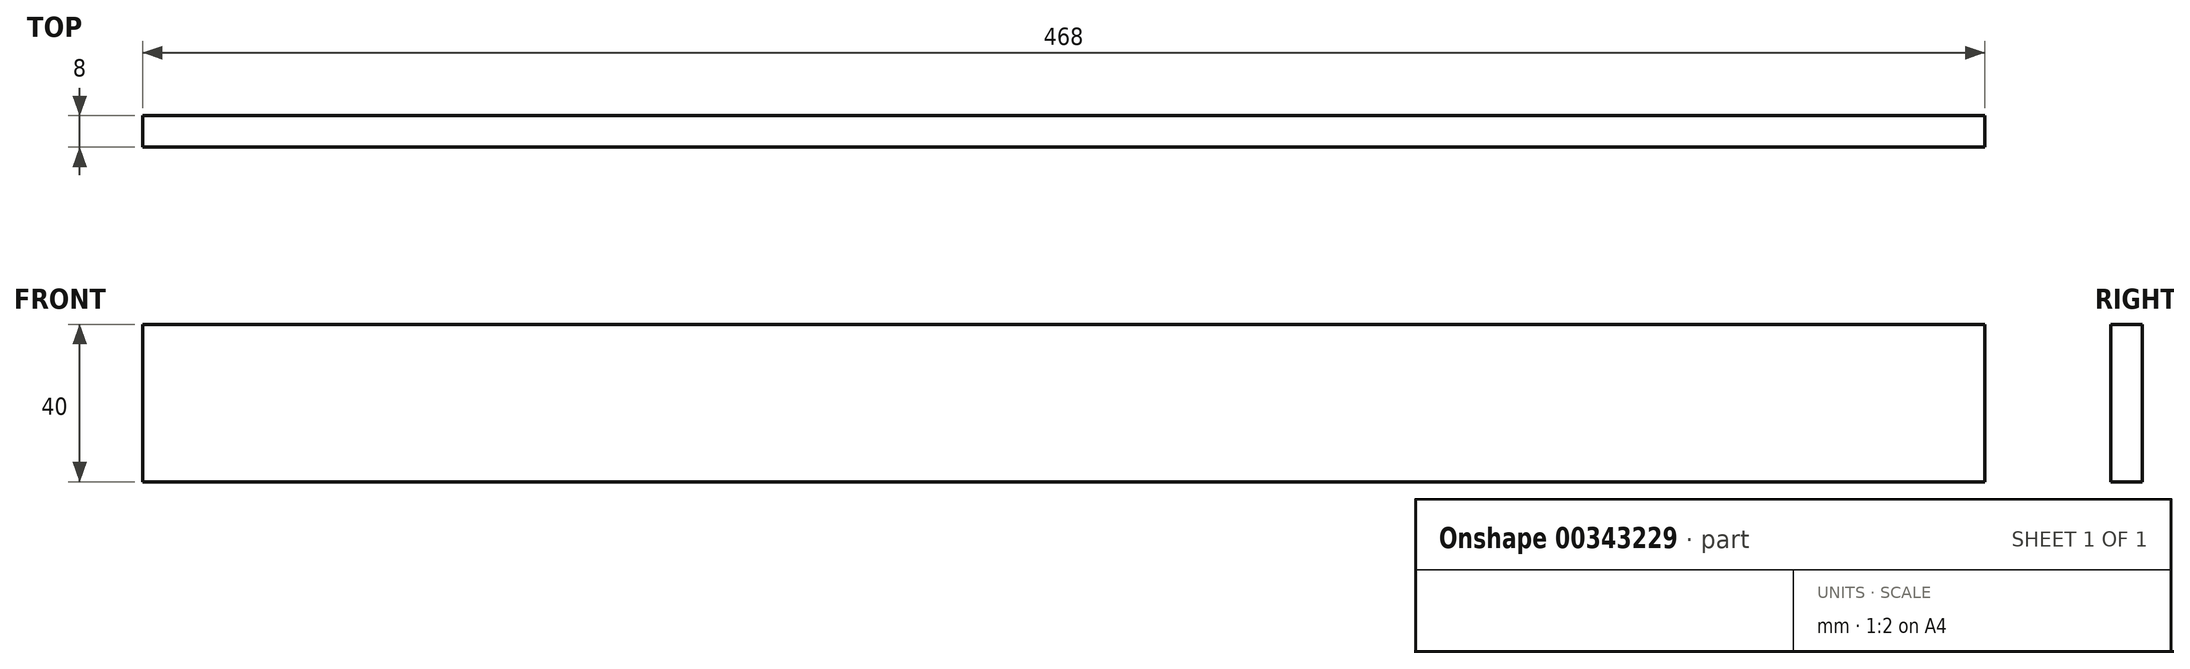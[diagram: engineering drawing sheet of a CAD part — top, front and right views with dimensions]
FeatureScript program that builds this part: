
annotation { "Feature Type Name" : "Feature", "Feature Type Description" : "" }
export const myFeature = defineFeature(function(context is Context, id is Id, definition is map)
    precondition{}
    {
        {
            var Q0;
            Q0=qCreatedBy(makeId("Front.planeOp"),FACE);
            var sketch = newSketch(context, id + "F0", { "sketchPlane" : qUnion([Q0])});
            skLineSegment(sketch, "E0.bottom", {"start": v(234, -20) * mm, "end": v(-234, -20) * mm});
            skLineSegment(sketch, "E0.top", {"start": v(234, 20) * mm, "end": v(-234, 20) * mm});
            skLineSegment(sketch, "E0.left", {"start": v(234, -20) * mm, "end": v(234, 20) * mm});
            skLineSegment(sketch, "E0.right", {"start": v(-234, -20) * mm, "end": v(-234, 20) * mm});
            skPoint(sketch, "E0.middle", {"position": v(0, 0) * mm});
            skSolve(sketch);
        }
        {
            var Q0;
            Q0=makeQuery(id+"F0.imprint","IMPRINT",FACE,{"disambiguationData":[TD([[makeQuery(id+"F0.imprint","IMPRINT",EDGE,{"derivedFrom":sQuery(id+"F0.wireOp",EDGE,"E0.bottom")}),-1.0]])]});
            extrude(context, id + "F1", {"entities" : qUnion([Q0]), "depth" : 8 * mm});
        }
    });
